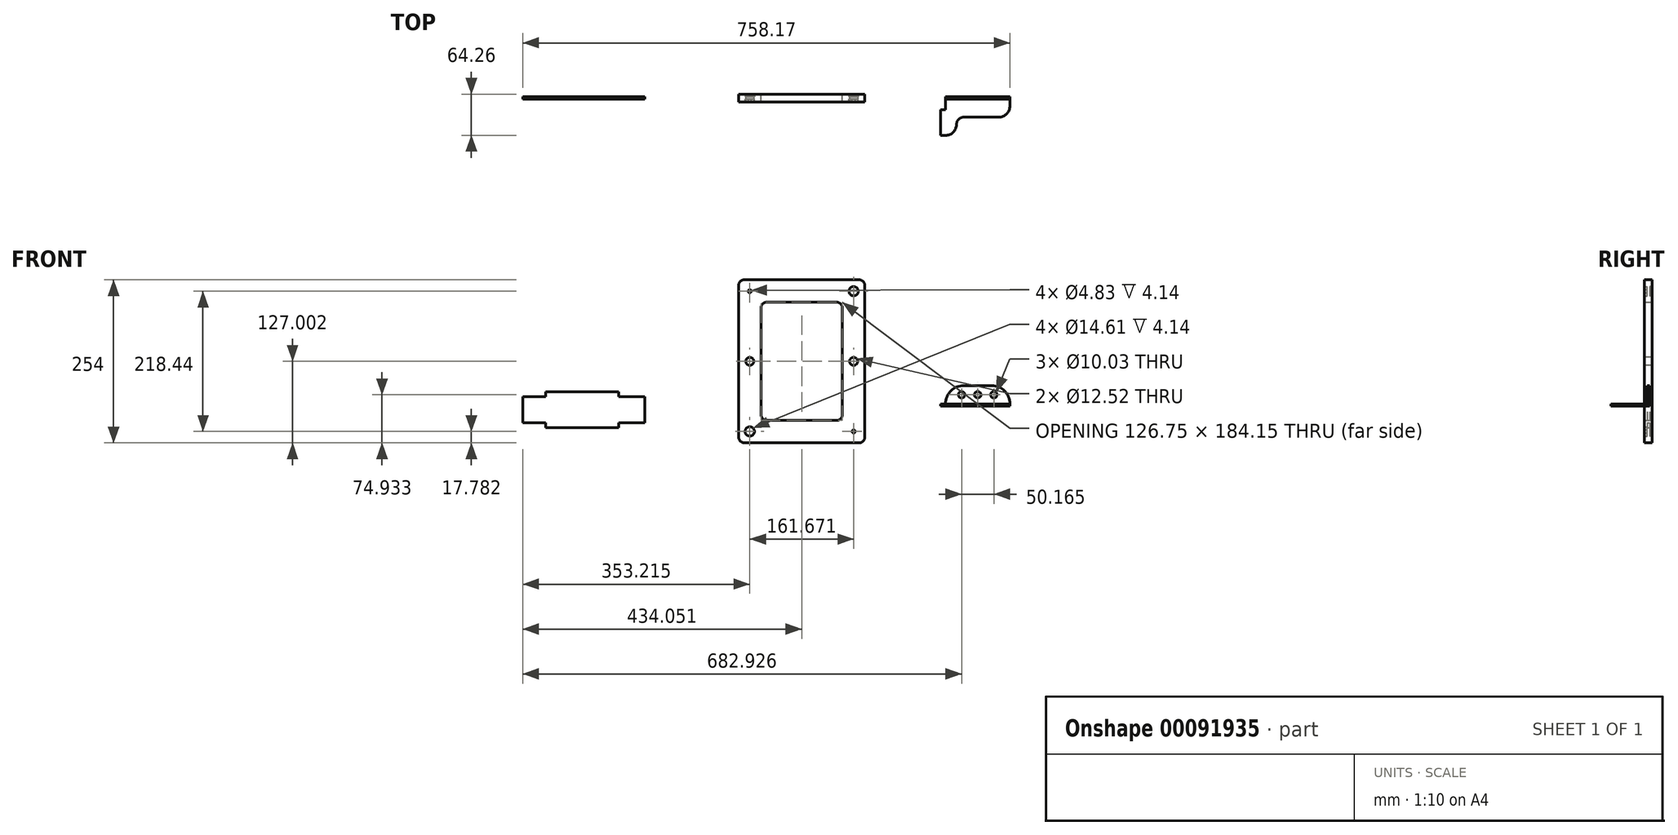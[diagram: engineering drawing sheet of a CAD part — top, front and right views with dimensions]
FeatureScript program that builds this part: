
annotation { "Feature Type Name" : "Feature", "Feature Type Description" : "" }
export const myFeature = defineFeature(function(context is Context, id is Id, definition is map)
    precondition{}
    {
        {
            var Q0;
            Q0=qCreatedBy(makeId("Front.planeOp"),FACE);
            var sketch = newSketch(context, id + "F0", { "sketchPlane" : qUnion([Q0])});
            skLineSegment(sketch, "E0.bottom", {"start": v(-106.17, 157.3) * mm, "end": v(90.43, 157.3) * mm});
            skLineSegment(sketch, "E0.top", {"start": v(-106.17, -96.7) * mm, "end": v(90.43, -96.7) * mm});
            skLineSegment(sketch, "E0.left", {"start": v(-106.17, 157.3) * mm, "end": v(-106.17, -96.7) * mm});
            skLineSegment(sketch, "E0.right", {"start": v(90.43, 157.3) * mm, "end": v(90.43, -96.7) * mm});
            skLineSegment(sketch, "E1.0", {"start": v(-71.24, 122.37) * mm, "end": v(55.5, 122.37) * mm});
            skLineSegment(sketch, "E1.1", {"start": v(-71.24, 122.37) * mm, "end": v(-71.24, -61.78) * mm});
            skLineSegment(sketch, "E1.2", {"start": v(-71.24, -61.78) * mm, "end": v(55.5, -61.78) * mm});
            skLineSegment(sketch, "E1.3", {"start": v(55.5, 122.37) * mm, "end": v(55.5, -61.78) * mm});
            skSolve(sketch);
        }
        {
            var Q0;
            Q0=makeQuery(id+"F0.imprint","IMPRINT",FACE,{"disambiguationData":[TD([[makeQuery(id+"F0.imprint","IMPRINT",EDGE,{"derivedFrom":sQuery(id+"F0.wireOp",EDGE,"E0.bottom")}),-1.0]])]});
            extrude(context, id + "F1", {"entities" : qUnion([Q0]), "depth" : 3.8 * mm});
        }
        {
            var Q0;
            Q0=makeQuery(id+"F1.opExtrude","SWEPT_EDGE",EDGE,{"disambiguationData":[OSD([sQuery(id+"F0.wireOp",EDGE,"E0.bottom"),sQuery(id+"F0.wireOp",EDGE,"E0.left")])]});
            var Q1;
            Q1=makeQuery(id+"F1.opExtrude","SWEPT_EDGE",EDGE,{"disambiguationData":[OSD([sQuery(id+"F0.wireOp",EDGE,"E0.bottom"),sQuery(id+"F0.wireOp",EDGE,"E0.right")])]});
            var Q2;
            Q2=makeQuery(id+"F1.opExtrude","SWEPT_EDGE",EDGE,{"disambiguationData":[OSD([sQuery(id+"F0.wireOp",EDGE,"E0.top"),sQuery(id+"F0.wireOp",EDGE,"E0.right")])]});
            var Q3;
            Q3=makeQuery(id+"F1.opExtrude","SWEPT_EDGE",EDGE,{"disambiguationData":[OSD([sQuery(id+"F0.wireOp",EDGE,"E0.top"),sQuery(id+"F0.wireOp",EDGE,"E0.left")])]});
            var Q4;
            Q4=makeQuery(id+"F1.opExtrude","SWEPT_EDGE",EDGE,{"disambiguationData":[OSD([sQuery(id+"F0.wireOp",EDGE,"E1.1"),sQuery(id+"F0.wireOp",EDGE,"E1.2")])]});
            var Q5;
            Q5=makeQuery(id+"F1.opExtrude","SWEPT_EDGE",EDGE,{"disambiguationData":[OSD([sQuery(id+"F0.wireOp",EDGE,"E1.2"),sQuery(id+"F0.wireOp",EDGE,"E1.3")])]});
            var Q6;
            Q6=makeQuery(id+"F1.opExtrude","SWEPT_EDGE",EDGE,{"disambiguationData":[OSD([sQuery(id+"F0.wireOp",EDGE,"E1.0"),sQuery(id+"F0.wireOp",EDGE,"E1.3")])]});
            var Q7;
            Q7=makeQuery(id+"F1.opExtrude","SWEPT_EDGE",EDGE,{"disambiguationData":[OSD([sQuery(id+"F0.wireOp",EDGE,"E1.0"),sQuery(id+"F0.wireOp",EDGE,"E1.1")])]});
            fillet(context, id + "F2", {"entities" : qUnion([Q0, Q1, Q2, Q3, Q4, Q5, Q6, Q7]), "radius" : 9.21 * mm, "tangentPropagation" : true, "allowEdgeOverflow" : false});
        }
        {
            var Q0;
            Q0=makeQuery(id+"F1.opExtrude","CAP_FACE",FACE,{"disambiguationData":[OSD([sQuery(id+"F0.wireOp",EDGE,"E0.bottom"),sQuery(id+"F0.wireOp",EDGE,"E0.top"),sQuery(id+"F0.wireOp",EDGE,"E0.left"),sQuery(id+"F0.wireOp",EDGE,"E0.right"),sQuery(id+"F0.wireOp",EDGE,"E1.0"),sQuery(id+"F0.wireOp",EDGE,"E1.1"),sQuery(id+"F0.wireOp",EDGE,"E1.2"),sQuery(id+"F0.wireOp",EDGE,"E1.3")])],"isStart":false});
            var sketch = newSketch(context, id + "F3", { "sketchPlane" : qUnion([Q0])});
            skLineSegment(sketch, "E2.0", {"start": v(-71.24, 113.15) * mm, "end": v(-71.24, -52.57) * mm});
            skLineSegment(sketch, "E3", {"start": v(-71.24, 30.3) * mm, "end": v(-106.17, 30.3) * mm, "construction": true});
            skCircle(sketch, "E4", {"center": v(-88.7, 30.3) * mm, "radius": 6.26 * mm});
            skLineSegment(sketch, "E5.0", {"start": v(55.5, 113.15) * mm, "end": v(55.5, -52.57) * mm});
            skLineSegment(sketch, "E6.0", {"start": v(-62.03, 122.37) * mm, "end": v(46.3, 122.37) * mm});
            skLineSegment(sketch, "E7", {"start": v(-7.87, 122.37) * mm, "end": v(-7.87, -61.78) * mm, "construction": true});
            skCircle(sketch, "E8.MirrorC", {"center": v(72.97, 30.3) * mm, "radius": 6.26 * mm});
            skLineSegment(sketch, "E9.MirrorCS", {"start": v(-7.87, -61.78) * mm, "end": v(-7.87, 122.37) * mm, "construction": true});
            skSolve(sketch);
        }
        {
            var Q0;
            Q0 = qSketchRegion(id + "F3", true);
            var Q1;
            Q1=makeQuery(id+"F1.opExtrude","CAP_FACE",FACE,{"disambiguationData":[OSD([sQuery(id+"F0.wireOp",EDGE,"E0.bottom"),sQuery(id+"F0.wireOp",EDGE,"E0.top"),sQuery(id+"F0.wireOp",EDGE,"E0.left"),sQuery(id+"F0.wireOp",EDGE,"E0.right"),sQuery(id+"F0.wireOp",EDGE,"E1.0"),sQuery(id+"F0.wireOp",EDGE,"E1.1"),sQuery(id+"F0.wireOp",EDGE,"E1.2"),sQuery(id+"F0.wireOp",EDGE,"E1.3")])],"isStart":true});
            extrude(context, id + "F4", {"entities" : qUnion([Q0]), "operationType" : NewBodyOperationType.REMOVE, "endBound" : BoundingType.UP_TO_SURFACE, "oppositeDirection" : true, "endBoundEntityFace" : qUnion([Q1]), "depth" : 25.4 * mm});
        }
        {
            var Q0;
            Q0=qCreatedBy(makeId("Front.planeOp"),FACE);
            var sketch = newSketch(context, id + "F5", { "sketchPlane" : qUnion([Q0])});
            skLineSegment(sketch, "E10.bottom", {"start": v(-406.36, -17.5) * mm, "end": v(-292.67, -17.5) * mm});
            skLineSegment(sketch, "E10.top", {"start": v(-406.36, -72.93) * mm, "end": v(-292.67, -72.93) * mm});
            skLineSegment(sketch, "E10.left", {"start": v(-406.36, -17.5) * mm, "end": v(-406.36, -72.93) * mm});
            skLineSegment(sketch, "E10.right", {"start": v(-292.67, -17.5) * mm, "end": v(-292.67, -72.93) * mm});
            skSolve(sketch);
        }
        {
            var Q0;
            Q0=makeQuery(id+"F5.imprint","IMPRINT",FACE,{"disambiguationData":[TD([[makeQuery(id+"F5.imprint","IMPRINT",EDGE,{"derivedFrom":sQuery(id+"F5.wireOp",EDGE,"E10.bottom")}),-1.0]])]});
            extrude(context, id + "F6", {"entities" : qUnion([Q0]), "depth" : 3.56 * mm});
        }
        {
            var Q0;
            Q0=qCreatedBy(makeId("Front.planeOp"),FACE);
            var sketch = newSketch(context, id + "F7", { "sketchPlane" : qUnion([Q0])});
            skLineSegment(sketch, "E11.bottom", {"start": v(215.92, -7.55) * mm, "end": v(316.25, -7.55) * mm});
            skLineSegment(sketch, "E11.top", {"start": v(215.92, -36) * mm, "end": v(316.25, -36) * mm});
            skLineSegment(sketch, "E11.left", {"start": v(215.92, -7.55) * mm, "end": v(215.92, -36) * mm});
            skLineSegment(sketch, "E11.right", {"start": v(316.25, -7.55) * mm, "end": v(316.25, -36) * mm});
            skSolve(sketch);
        }
        {
            var Q0;
            Q0=makeQuery(id+"F7.imprint","IMPRINT",FACE,{"disambiguationData":[TD([[makeQuery(id+"F7.imprint","IMPRINT",EDGE,{"derivedFrom":sQuery(id+"F7.wireOp",EDGE,"E11.bottom")}),-1.0]])]});
            extrude(context, id + "F8", {"entities" : qUnion([Q0]), "depth" : 3.56 * mm});
        }
        {
            var Q0;
            Q0=makeQuery(id+"F8.opExtrude","SWEPT_EDGE",EDGE,{"disambiguationData":[OSD([sQuery(id+"F7.wireOp",EDGE,"E11.bottom"),sQuery(id+"F7.wireOp",EDGE,"E11.left")])]});
            var Q1;
            Q1=makeQuery(id+"F8.opExtrude","SWEPT_EDGE",EDGE,{"disambiguationData":[OSD([sQuery(id+"F7.wireOp",EDGE,"E11.bottom"),sQuery(id+"F7.wireOp",EDGE,"E11.right")])]});
            fillet(context, id + "F9", {"entities" : qUnion([Q0, Q1]), "radius" : 28.45 * mm, "tangentPropagation" : true, "allowEdgeOverflow" : false});
        }
        {
            var Q0;
            Q0=makeQuery(id+"F8.opExtrude","CAP_FACE",FACE,{"disambiguationData":[OSD([sQuery(id+"F7.wireOp",EDGE,"E11.bottom"),sQuery(id+"F7.wireOp",EDGE,"E11.top"),sQuery(id+"F7.wireOp",EDGE,"E11.left"),sQuery(id+"F7.wireOp",EDGE,"E11.right")])],"isStart":false});
            var sketch = newSketch(context, id + "F10", { "sketchPlane" : qUnion([Q0])});
            skLineSegment(sketch, "E12", {"start": v(215.92, -36) * mm, "end": v(215.92, -7.55) * mm, "construction": true});
            skLineSegment(sketch, "E13", {"start": v(316.25, -36) * mm, "end": v(316.25, -7.55) * mm, "construction": true});
            skLineSegment(sketch, "E14", {"start": v(215.92, -21.78) * mm, "end": v(316.25, -21.78) * mm, "construction": true});
            skLineSegment(sketch, "E15", {"start": v(266.09, -7.55) * mm, "end": v(266.09, -36) * mm, "construction": true});
            skCircle(sketch, "E16", {"center": v(266.09, -21.78) * mm, "radius": 5.02 * mm});
            skLineSegment(sketch, "E17", {"start": v(266.09, -21.78) * mm, "end": v(316.25, -21.78) * mm, "construction": true});
            skCircle(sketch, "E18", {"center": v(291.17, -21.78) * mm, "radius": 5.02 * mm});
            skCircle(sketch, "E19.MirrorC", {"center": v(241, -21.78) * mm, "radius": 5.02 * mm});
            skSolve(sketch);
        }
        {
            var Q0;
            Q0 = qSketchRegion(id + "F10", true);
            var Q1;
            Q1=makeQuery(id+"F8.opExtrude","CAP_FACE",FACE,{"disambiguationData":[OSD([sQuery(id+"F7.wireOp",EDGE,"E11.bottom"),sQuery(id+"F7.wireOp",EDGE,"E11.top"),sQuery(id+"F7.wireOp",EDGE,"E11.left"),sQuery(id+"F7.wireOp",EDGE,"E11.right")])],"isStart":true});
            extrude(context, id + "F11", {"entities" : qUnion([Q0]), "operationType" : NewBodyOperationType.REMOVE, "endBound" : BoundingType.UP_TO_SURFACE, "oppositeDirection" : true, "endBoundEntityFace" : qUnion([Q1]), "depth" : 25.4 * mm});
        }
        {
            var Q0;
            Q0=makeQuery(id+"F6.opExtrude","SWEPT_FACE",FACE,{"disambiguationData":[OSD([sQuery(id+"F5.wireOp",EDGE,"E10.left")])]});
            var sketch = newSketch(context, id + "F12", { "sketchPlane" : qUnion([Q0])});
            skLineSegment(sketch, "E20.0", {"start": v(3.56, -65.3) * mm, "end": v(0, -65.3) * mm});
            skLineSegment(sketch, "E21.0", {"start": v(3.56, -25.12) * mm, "end": v(0, -25.12) * mm});
            skLineSegment(sketch, "E22", {"start": v(3.56, -25.12) * mm, "end": v(3.56, -65.3) * mm});
            skLineSegment(sketch, "E23", {"start": v(0, -65.3) * mm, "end": v(0, -25.12) * mm});
            skSolve(sketch);
        }
        {
            var Q0;
            Q0 = qSketchRegion(id + "F12", true);
            extrude(context, id + "F13", {"entities" : qUnion([Q0]), "operationType" : NewBodyOperationType.ADD, "depth" : 35.56 * mm});
        }
        {
            var Q0;
            Q0=makeQuery(id+"F6.opExtrude","SWEPT_FACE",FACE,{"disambiguationData":[OSD([sQuery(id+"F5.wireOp",EDGE,"E10.right")])]});
            var sketch = newSketch(context, id + "F14", { "sketchPlane" : qUnion([Q0])});
            skLineSegment(sketch, "E24.0", {"start": v(-3.56, -65.3) * mm, "end": v(0, -65.3) * mm});
            skLineSegment(sketch, "E25.0", {"start": v(-3.56, -25.12) * mm, "end": v(0, -25.12) * mm});
            skLineSegment(sketch, "E26", {"start": v(0, -25.12) * mm, "end": v(0, -65.3) * mm});
            skLineSegment(sketch, "E27", {"start": v(-3.56, -65.3) * mm, "end": v(-3.56, -25.12) * mm});
            skSolve(sketch);
        }
        {
            var Q0;
            Q0=makeQuery(id+"F14.imprint","IMPRINT",FACE,{"disambiguationData":[TD([[makeQuery(id+"F14.imprint","IMPRINT",EDGE,{"derivedFrom":sQuery(id+"F14.wireOp",EDGE,"E24.0")}),1.0]])]});
            extrude(context, id + "F15", {"entities" : qUnion([Q0]), "operationType" : NewBodyOperationType.ADD, "depth" : 40.64 * mm});
        }
        {
            var Q0;
            Q0=makeQuery(id+"F1.opExtrude","CAP_FACE",FACE,{"disambiguationData":[OSD([sQuery(id+"F0.wireOp",EDGE,"E0.bottom"),sQuery(id+"F0.wireOp",EDGE,"E0.top"),sQuery(id+"F0.wireOp",EDGE,"E0.left"),sQuery(id+"F0.wireOp",EDGE,"E0.right"),sQuery(id+"F0.wireOp",EDGE,"E1.0"),sQuery(id+"F0.wireOp",EDGE,"E1.1"),sQuery(id+"F0.wireOp",EDGE,"E1.2"),sQuery(id+"F0.wireOp",EDGE,"E1.3")])],"isStart":true});
            var sketch = newSketch(context, id + "F16", { "sketchPlane" : qUnion([Q0])});
            skCircle(sketch, "E28", {"center": v(88.7, 139.51) * mm, "radius": 7.3 * mm});
            skLineSegment(sketch, "E29.0", {"start": v(71.24, 113.15) * mm, "end": v(71.24, -52.57) * mm});
            skLineSegment(sketch, "E30.0", {"start": v(62.03, 122.37) * mm, "end": v(-46.3, 122.37) * mm});
            skLineSegment(sketch, "E31", {"start": v(71.24, 30.3) * mm, "end": v(106.17, 30.3) * mm, "construction": true});
            skLineSegment(sketch, "E32", {"start": v(7.87, 122.37) * mm, "end": v(7.87, -61.78) * mm, "construction": true});
            skCircle(sketch, "E33.MirrorC", {"center": v(88.7, -78.93) * mm, "radius": 7.3 * mm});
            skCircle(sketch, "E34.MirrorC", {"center": v(-72.97, 139.51) * mm, "radius": 7.3 * mm});
            skCircle(sketch, "E35.MirrorC", {"center": v(-72.97, -78.93) * mm, "radius": 7.3 * mm});
            skCircle(sketch, "E36", {"center": v(88.7, 139.51) * mm, "radius": 2.41 * mm});
            skCircle(sketch, "E37.MirrorC", {"center": v(88.7, -78.93) * mm, "radius": 2.41 * mm});
            skCircle(sketch, "E38.MirrorC", {"center": v(-72.97, -78.93) * mm, "radius": 2.41 * mm});
            skCircle(sketch, "E39.MirrorC", {"center": v(-72.97, 139.51) * mm, "radius": 2.41 * mm});
            skSolve(sketch);
        }
        {
            var Q0;
            Q0=makeQuery(id+"F16.imprint","IMPRINT",FACE,{"disambiguationData":[TD([[makeQuery(id+"F16.imprint","IMPRINT",EDGE,{"derivedFrom":sQuery(id+"F16.wireOp",EDGE,"E34.MirrorC")}),-1.0]])]});
            var Q1;
            Q1=makeQuery(id+"F16.imprint","IMPRINT",FACE,{"disambiguationData":[TD([[makeQuery(id+"F16.imprint","IMPRINT",EDGE,{"derivedFrom":sQuery(id+"F16.wireOp",EDGE,"E28")}),1.0]])]});
            var Q2;
            Q2=makeQuery(id+"F16.imprint","IMPRINT",FACE,{"disambiguationData":[TD([[makeQuery(id+"F16.imprint","IMPRINT",EDGE,{"derivedFrom":sQuery(id+"F16.wireOp",EDGE,"E33.MirrorC")}),-1.0]])]});
            var Q3;
            Q3=makeQuery(id+"F16.imprint","IMPRINT",FACE,{"disambiguationData":[TD([[makeQuery(id+"F16.imprint","IMPRINT",EDGE,{"derivedFrom":sQuery(id+"F16.wireOp",EDGE,"E35.MirrorC")}),1.0]])]});
            extrude(context, id + "F17", {"entities" : qUnion([Q0, Q1, Q2, Q3]), "operationType" : NewBodyOperationType.ADD, "depth" : 4.14 * mm});
        }
        {
            var Q0;
            Q0=makeQuery(id+"F1.opExtrude","CAP_FACE",FACE,{"disambiguationData":[OSD([sQuery(id+"F0.wireOp",EDGE,"E0.bottom"),sQuery(id+"F0.wireOp",EDGE,"E0.top"),sQuery(id+"F0.wireOp",EDGE,"E0.left"),sQuery(id+"F0.wireOp",EDGE,"E0.right"),sQuery(id+"F0.wireOp",EDGE,"E1.0"),sQuery(id+"F0.wireOp",EDGE,"E1.1"),sQuery(id+"F0.wireOp",EDGE,"E1.2"),sQuery(id+"F0.wireOp",EDGE,"E1.3")])],"isStart":false});
            var sketch = newSketch(context, id + "F18", { "sketchPlane" : qUnion([Q0])});
            skCircle(sketch, "E40.0", {"center": v(72.97, 30.3) * mm, "radius": 6.26 * mm});
            skCircle(sketch, "E41", {"center": v(72.97, -78.93) * mm, "radius": 7.3 * mm});
            skCircle(sketch, "E42", {"center": v(72.97, -78.93) * mm, "radius": 2.41 * mm});
            skLineSegment(sketch, "E43", {"start": v(-7.87, -61.78) * mm, "end": v(-7.87, 122.37) * mm, "construction": true});
            skLineSegment(sketch, "E44", {"start": v(90.43, 30.3) * mm, "end": v(55.5, 30.3) * mm, "construction": true});
            skCircle(sketch, "E45.MirrorC", {"center": v(-88.7, -78.93) * mm, "radius": 7.3 * mm});
            skCircle(sketch, "E46.MirrorC", {"center": v(-88.7, -78.93) * mm, "radius": 2.41 * mm});
            skCircle(sketch, "E47.MirrorC", {"center": v(72.97, 139.51) * mm, "radius": 7.3 * mm});
            skCircle(sketch, "E48.MirrorC", {"center": v(72.97, 139.51) * mm, "radius": 2.41 * mm});
            skCircle(sketch, "E49.MirrorC", {"center": v(-88.7, 139.51) * mm, "radius": 7.3 * mm});
            skCircle(sketch, "E50.MirrorC", {"center": v(-88.7, 139.51) * mm, "radius": 2.41 * mm});
            skSolve(sketch);
        }
        {
            var Q0;
            Q0=makeQuery(id+"F18.imprint","IMPRINT",FACE,{"disambiguationData":[TD([[makeQuery(id+"F18.imprint","IMPRINT",EDGE,{"derivedFrom":sQuery(id+"F18.wireOp",EDGE,"E47.MirrorC")}),-1.0]])]});
            var Q1;
            Q1=makeQuery(id+"F18.imprint","IMPRINT",FACE,{"disambiguationData":[TD([[makeQuery(id+"F18.imprint","IMPRINT",EDGE,{"derivedFrom":sQuery(id+"F18.wireOp",EDGE,"E49.MirrorC")}),1.0]])]});
            var Q2;
            Q2=makeQuery(id+"F18.imprint","IMPRINT",FACE,{"disambiguationData":[TD([[makeQuery(id+"F18.imprint","IMPRINT",EDGE,{"derivedFrom":sQuery(id+"F18.wireOp",EDGE,"E45.MirrorC")}),-1.0]])]});
            var Q3;
            Q3=makeQuery(id+"F18.imprint","IMPRINT",FACE,{"disambiguationData":[TD([[makeQuery(id+"F18.imprint","IMPRINT",EDGE,{"derivedFrom":sQuery(id+"F18.wireOp",EDGE,"E41")}),1.0]])]});
            extrude(context, id + "F19", {"entities" : qUnion([Q0, Q1, Q2, Q3]), "operationType" : NewBodyOperationType.ADD, "depth" : 4.14 * mm});
        }
        {
            var Q0;
            Q0=makeQuery(id+"F8.opExtrude","SWEPT_FACE",FACE,{"disambiguationData":[OSD([sQuery(id+"F7.wireOp",EDGE,"E11.top")])]});
            var sketch = newSketch(context, id + "F20", { "sketchPlane" : qUnion([Q0])});
            skLineSegment(sketch, "E51", {"start": v(316.25, 0) * mm, "end": v(316.25, 31.75) * mm});
            skLineSegment(sketch, "E52", {"start": v(316.25, 31.75) * mm, "end": v(244.48, 31.75) * mm});
            skLineSegment(sketch, "E53", {"start": v(215.92, 31.75) * mm, "end": v(215.92, 0) * mm, "construction": true});
            skArc(sketch, "E54", {"start": v(244.48, 31.75) * mm, "mid": v(236.18, 35.32) * mm, "end": v(233.07, 43.8) * mm});
            skArc(sketch, "E55", {"start": v(233.07, 43.8) * mm, "mid": v(227.76, 55.39) * mm, "end": v(215.92, 60.12) * mm});
            skLineSegment(sketch, "E56", {"start": v(215.92, 0) * mm, "end": v(215.92, 60.12) * mm});
            skLineSegment(sketch, "E57", {"start": v(215.92, 0) * mm, "end": v(316.25, 0) * mm});
            skSolve(sketch);
        }
        {
            var Q0;
            Q0 = qSketchRegion(id + "F20", true);
            extrude(context, id + "F21", {"entities" : qUnion([Q0]), "depth" : 3.56 * mm});
        }
        {
            var Q0;
            Q0=makeQuery(id+"F21.opExtrude","SWEPT_FACE",FACE,{"disambiguationData":[OSD([sQuery(id+"F20.wireOp",EDGE,"E56")])]});
            var sketch = newSketch(context, id + "F22", { "sketchPlane" : qUnion([Q0])});
            skLineSegment(sketch, "E58.bottom", {"start": v(60.12, -36) * mm, "end": v(19.93, -36) * mm});
            skLineSegment(sketch, "E58.top", {"start": v(60.12, -39.56) * mm, "end": v(19.93, -39.56) * mm});
            skLineSegment(sketch, "E58.left", {"start": v(60.12, -36) * mm, "end": v(60.12, -39.56) * mm});
            skLineSegment(sketch, "E58.right", {"start": v(19.93, -36) * mm, "end": v(19.93, -39.56) * mm});
            skSolve(sketch);
        }
        {
            var Q0;
            Q0 = qSketchRegion(id + "F22", true);
            extrude(context, id + "F23", {"entities" : qUnion([Q0]), "operationType" : NewBodyOperationType.ADD, "depth" : 7.62 * mm});
        }
        {
            var Q0;
            Q0=makeQuery(id+"F21.opExtrude","SWEPT_EDGE",EDGE,{"disambiguationData":[OSD([sQuery(id+"F20.wireOp",EDGE,"E51"),sQuery(id+"F20.wireOp",EDGE,"E52")])]});
            fillet(context, id + "F24", {"entities" : qUnion([Q0]), "radius" : 17.62 * mm, "tangentPropagation" : true, "allowEdgeOverflow" : false});
        }
    });
